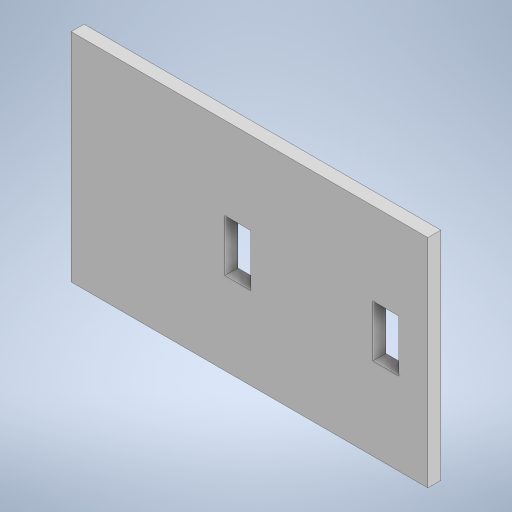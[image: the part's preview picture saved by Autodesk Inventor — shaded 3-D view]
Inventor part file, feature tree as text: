
AUTODESK INVENTOR PART (.ipt)
format: ipt  version: 2024 (Build 280153000, 153)  size: 202,752 bytes
history: native  units: mm
features: extrude x2, sketch x2
ambient origin geometry x8: Origin, YZ Plane, XZ Plane, XY Plane, X Axis, Y Axis, Z Axis, Center Point
bodies: Solid1 (feature_tree)
feature tree (4):
  extrude  "Extrusion1"  Depth=2.5mm TaperAngle=0.0deg
  extrude  "Extrusion2"  [1 undecoded]
  sketch  "Sketch1"  dims[d3=2.5mm d4=0.0mm d11=2.5mm d12=0.0mm]
  sketch  "Sketch2"
note: 1 required parameter value undecoded (feature->parameter linkage not recoverable at this tier; creation-order binding heuristic only, values carry confidence <= 0.55)
